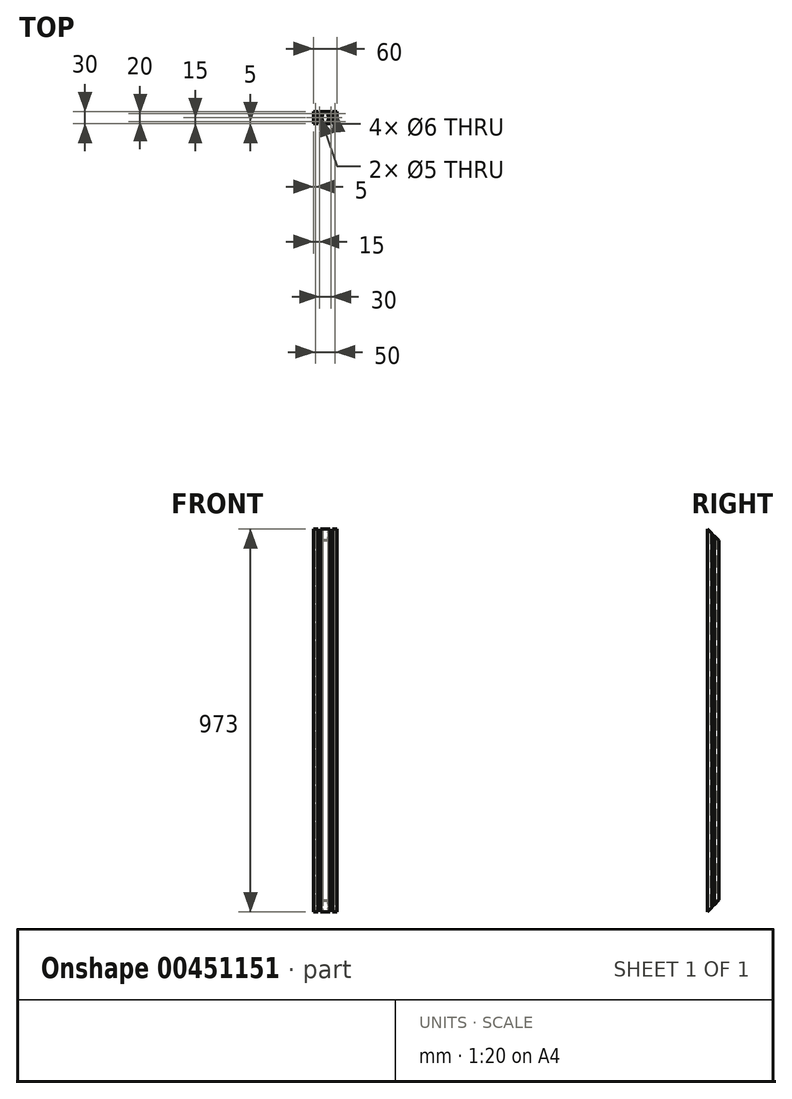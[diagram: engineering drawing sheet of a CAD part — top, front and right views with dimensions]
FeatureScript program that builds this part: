
annotation { "Feature Type Name" : "Feature", "Feature Type Description" : "" }
export const myFeature = defineFeature(function(context is Context, id is Id, definition is map)
    precondition{}
    {
        {
            var Q0;
            Q0=qCreatedBy(makeId("Top.planeOp"),FACE);
            var sketch = newSketch(context, id + "F0", { "sketchPlane" : qUnion([Q0])});
            skLineSegment(sketch, "E0.bottom", {"start": v(30, -15) * mm, "end": v(-30, -15) * mm});
            skLineSegment(sketch, "E0.top", {"start": v(30, 15) * mm, "end": v(-30, 15) * mm});
            skLineSegment(sketch, "E0.left", {"start": v(30, -15) * mm, "end": v(30, 15) * mm});
            skLineSegment(sketch, "E0.right", {"start": v(-30, -15) * mm, "end": v(-30, 15) * mm});
            skPoint(sketch, "E0.middle", {"position": v(0, 0) * mm});
            skLineSegment(sketch, "E1.top", {"start": v(-11.85, 15) * mm, "end": v(-18.15, 15) * mm});
            skLineSegment(sketch, "E1.left", {"start": v(-11.85, 12.5) * mm, "end": v(-11.85, 15) * mm});
            skLineSegment(sketch, "E1.right", {"start": v(-18.15, 12.5) * mm, "end": v(-18.15, 15) * mm});
            skPoint(sketch, "E1.middle", {"position": v(-15, 13.75) * mm});
            skLineSegment(sketch, "E2.bottom", {"start": v(-9.85, 12.5) * mm, "end": v(-11.85, 12.5) * mm});
            skLineSegment(sketch, "E2.left", {"start": v(-9.85, 12.5) * mm, "end": v(-9.85, 6.55) * mm});
            skLineSegment(sketch, "E2.right", {"start": v(-20.15, 12.5) * mm, "end": v(-20.15, 6.55) * mm});
            skPoint(sketch, "E2.middle", {"position": v(-15, 9.52) * mm});
            skArc(sketch, "E3", {"start": v(-20.15, 6.55) * mm, "mid": v(-15, 4.5) * mm, "end": v(-9.85, 6.55) * mm});
            skPoint(sketch, "E4.MirrorP", {"position": v(15, 9.52) * mm});
            skPoint(sketch, "E5.MirrorP", {"position": v(15, 13.75) * mm});
            skLineSegment(sketch, "E6.MirrorCS", {"start": v(11.85, 12.5) * mm, "end": v(11.85, 15) * mm});
            skLineSegment(sketch, "E7.MirrorCS", {"start": v(18.15, 12.5) * mm, "end": v(18.15, 15) * mm});
            skLineSegment(sketch, "E8.MirrorCS", {"start": v(9.85, 12.5) * mm, "end": v(11.85, 12.5) * mm});
            skLineSegment(sketch, "E9.MirrorCS", {"start": v(9.85, 12.5) * mm, "end": v(9.85, 6.55) * mm});
            skArc(sketch, "E10.MirrorCS", {"start": v(20.15, 6.55) * mm, "mid": v(15, 4.5) * mm, "end": v(9.85, 6.55) * mm});
            skLineSegment(sketch, "E11.MirrorCS", {"start": v(20.15, 12.5) * mm, "end": v(20.15, 6.55) * mm});
            skLineSegment(sketch, "E12.MirrorCS", {"start": v(11.85, 15) * mm, "end": v(18.15, 15) * mm});
            skLineSegment(sketch, "E13.trimOffspring", {"start": v(-18.15, 12.5) * mm, "end": v(-20.15, 12.5) * mm});
            skLineSegment(sketch, "E14.trimOffspring", {"start": v(18.15, 12.5) * mm, "end": v(20.15, 12.5) * mm});
            skCircle(sketch, "E15", {"center": v(-15, 0) * mm, "radius": 2.5 * mm});
            skCircle(sketch, "E16", {"center": v(-25, 10) * mm, "radius": 3 * mm});
            skCircle(sketch, "E17.MirrorC", {"center": v(25, 10) * mm, "radius": 3 * mm});
            skCircle(sketch, "E18.MirrorC", {"center": v(25, -10) * mm, "radius": 3 * mm});
            skCircle(sketch, "E19.MirrorC", {"center": v(-25, -10) * mm, "radius": 3 * mm});
            skCircle(sketch, "E20.MirrorC", {"center": v(15, 0) * mm, "radius": 2.5 * mm});
            skLineSegment(sketch, "E21", {"start": v(-7, 12.5) * mm, "end": v(0, 12.5) * mm});
            skLineSegment(sketch, "E22", {"start": v(-7, 12.5) * mm, "end": v(-7, 7) * mm});
            skLineSegment(sketch, "E23", {"start": v(-10, 0) * mm, "end": v(-7, 7) * mm});
            skLineSegment(sketch, "E24.MirrorCS", {"start": v(10, 0) * mm, "end": v(7, 7) * mm});
            skLineSegment(sketch, "E25.MirrorCS", {"start": v(7, 12.5) * mm, "end": v(0, 12.5) * mm});
            skLineSegment(sketch, "E26.MirrorCS", {"start": v(7, 12.5) * mm, "end": v(7, 7) * mm});
            skLineSegment(sketch, "E27.MirrorCS", {"start": v(-18.15, -12.5) * mm, "end": v(-20.15, -12.5) * mm});
            skLineSegment(sketch, "E28.MirrorCS", {"start": v(-9.85, -12.5) * mm, "end": v(-11.85, -12.5) * mm});
            skLineSegment(sketch, "E29.MirrorCS", {"start": v(-9.85, -12.5) * mm, "end": v(-9.85, -6.55) * mm});
            skPoint(sketch, "E30.MirrorP", {"position": v(-15, -13.75) * mm});
            skPoint(sketch, "E31.MirrorP", {"position": v(-15, -9.52) * mm});
            skLineSegment(sketch, "E32.MirrorCS", {"start": v(-18.15, -12.5) * mm, "end": v(-18.15, -15) * mm});
            skLineSegment(sketch, "E33.MirrorCS", {"start": v(-11.85, -15) * mm, "end": v(-18.15, -15) * mm});
            skLineSegment(sketch, "E34.MirrorCS", {"start": v(-20.15, -12.5) * mm, "end": v(-20.15, -6.55) * mm});
            skLineSegment(sketch, "E35.MirrorCS", {"start": v(-11.85, -12.5) * mm, "end": v(-11.85, -15) * mm});
            skArc(sketch, "E36.MirrorCS", {"start": v(-20.15, -6.55) * mm, "mid": v(-15, -4.5) * mm, "end": v(-9.85, -6.55) * mm});
            skLineSegment(sketch, "E37.MirrorCS", {"start": v(18.15, -12.5) * mm, "end": v(20.15, -12.5) * mm});
            skLineSegment(sketch, "E38.MirrorCS", {"start": v(9.85, -12.5) * mm, "end": v(11.85, -12.5) * mm});
            skPoint(sketch, "E39.MirrorP", {"position": v(15, -13.75) * mm});
            skPoint(sketch, "E40.MirrorP", {"position": v(15, -9.52) * mm});
            skLineSegment(sketch, "E41.MirrorCS", {"start": v(18.15, -12.5) * mm, "end": v(18.15, -15) * mm});
            skArc(sketch, "E42.MirrorCS", {"start": v(20.15, -6.55) * mm, "mid": v(15, -4.5) * mm, "end": v(9.85, -6.55) * mm});
            skLineSegment(sketch, "E43.MirrorCS", {"start": v(9.85, -12.5) * mm, "end": v(9.85, -6.55) * mm});
            skLineSegment(sketch, "E44.MirrorCS", {"start": v(11.85, -12.5) * mm, "end": v(11.85, -15) * mm});
            skLineSegment(sketch, "E45.MirrorCS", {"start": v(11.85, -15) * mm, "end": v(18.15, -15) * mm});
            skLineSegment(sketch, "E46.MirrorCS", {"start": v(20.15, -12.5) * mm, "end": v(20.15, -6.55) * mm});
            skLineSegment(sketch, "E47.MirrorCS", {"start": v(10, 0) * mm, "end": v(7, -7) * mm});
            skLineSegment(sketch, "E48.MirrorCS", {"start": v(7, -12.5) * mm, "end": v(7, -7) * mm});
            skLineSegment(sketch, "E49.MirrorCS", {"start": v(7, -12.5) * mm, "end": v(0, -12.5) * mm});
            skLineSegment(sketch, "E50.MirrorCS", {"start": v(-7, -12.5) * mm, "end": v(0, -12.5) * mm});
            skLineSegment(sketch, "E51.MirrorCS", {"start": v(-10, 0) * mm, "end": v(-7, -7) * mm});
            skLineSegment(sketch, "E52.MirrorCS", {"start": v(-7, -12.5) * mm, "end": v(-7, -7) * mm});
            skLineSegment(sketch, "E53.top", {"start": v(-30, 3.15) * mm, "end": v(-30, -3.15) * mm});
            skLineSegment(sketch, "E53.left", {"start": v(-27.5, 3.15) * mm, "end": v(-30, 3.15) * mm});
            skLineSegment(sketch, "E53.right", {"start": v(-27.5, -3.15) * mm, "end": v(-30, -3.15) * mm});
            skLineSegment(sketch, "E54.bottom", {"start": v(-27.5, 5.15) * mm, "end": v(-27.5, 3.15) * mm});
            skLineSegment(sketch, "E54.left", {"start": v(-27.5, 5.15) * mm, "end": v(-21.55, 5.15) * mm});
            skLineSegment(sketch, "E54.right", {"start": v(-27.5, -5.15) * mm, "end": v(-21.55, -5.15) * mm});
            skArc(sketch, "E55", {"start": v(-21.55, -5.15) * mm, "mid": v(-19.5, 0) * mm, "end": v(-21.55, 5.15) * mm});
            skLineSegment(sketch, "E56.trimOffspring", {"start": v(-27.5, -3.15) * mm, "end": v(-27.5, -5.15) * mm});
            skArc(sketch, "E57.MirrorCS", {"start": v(21.55, -5.15) * mm, "mid": v(19.5, 0) * mm, "end": v(21.55, 5.15) * mm});
            skLineSegment(sketch, "E58.MirrorCS", {"start": v(27.5, -5.15) * mm, "end": v(21.55, -5.15) * mm});
            skLineSegment(sketch, "E59.MirrorCS", {"start": v(30, 3.15) * mm, "end": v(30, -3.15) * mm});
            skLineSegment(sketch, "E60.MirrorCS", {"start": v(27.5, -3.15) * mm, "end": v(30, -3.15) * mm});
            skLineSegment(sketch, "E61.MirrorCS", {"start": v(27.5, 5.15) * mm, "end": v(27.5, 3.15) * mm});
            skLineSegment(sketch, "E62.MirrorCS", {"start": v(27.5, 3.15) * mm, "end": v(30, 3.15) * mm});
            skLineSegment(sketch, "E63.MirrorCS", {"start": v(27.5, 5.15) * mm, "end": v(21.55, 5.15) * mm});
            skLineSegment(sketch, "E64.MirrorCS", {"start": v(27.5, -3.15) * mm, "end": v(27.5, -5.15) * mm});
            skSolve(sketch);
        }
        {
            var Q0;
            {var subQ30=sQuery(id+"F0.wireOp",EDGE,"E1.left");Q0=makeQuery(id+"F0.imprint","IMPRINT",FACE,{"disambiguationData":[TD([[makeQuery(id+"F0.imprint","IMPRINT",EDGE,{"derivedFrom":subQ30}),-1.0]])]});}
            extrude(context, id + "F1", {"entities" : qUnion([Q0]), "offsetDistance" : 25 * mm, "depth" : 973 * mm});
        }
        {
            var Q0;
            Q0=makeQuery(id+"F1.opExtrude","SWEPT_EDGE",EDGE,{"disambiguationData":[OSD([sQuery(id+"F0.wireOp",EDGE,"E21"),sQuery(id+"F0.wireOp",EDGE,"E22")])]});
            var Q1;
            Q1=makeQuery(id+"F1.opExtrude","SWEPT_EDGE",EDGE,{"disambiguationData":[OSD([sQuery(id+"F0.wireOp",EDGE,"E25.MirrorCS"),sQuery(id+"F0.wireOp",EDGE,"E26.MirrorCS")])]});
            var Q2;
            Q2=makeQuery(id+"F1.opExtrude","SWEPT_EDGE",EDGE,{"disambiguationData":[OSD([sQuery(id+"F0.wireOp",EDGE,"840db5bc-c403-45cd-90c7-254e62d9e8c5.3.2"),sQuery(id+"F0.wireOp",EDGE,"840db5bc-c403-45cd-90c7-254e62d9e8c5.3.3")])]});
            var Q3;
            Q3=makeQuery(id+"F1.opExtrude","SWEPT_EDGE",EDGE,{"disambiguationData":[OSD([sQuery(id+"F0.wireOp",EDGE,"840db5bc-c403-45cd-90c7-254e62d9e8c5.3.4"),sQuery(id+"F0.wireOp",EDGE,"840db5bc-c403-45cd-90c7-254e62d9e8c5.3.5")])]});
            var Q4;
            Q4=makeQuery(id+"F1.opExtrude","SWEPT_EDGE",EDGE,{"disambiguationData":[OSD([sQuery(id+"F0.wireOp",EDGE,"840db5bc-c403-45cd-90c7-254e62d9e8c5.1.4"),sQuery(id+"F0.wireOp",EDGE,"840db5bc-c403-45cd-90c7-254e62d9e8c5.1.5")])]});
            var Q5;
            Q5=makeQuery(id+"F1.opExtrude","SWEPT_EDGE",EDGE,{"disambiguationData":[OSD([sQuery(id+"F0.wireOp",EDGE,"840db5bc-c403-45cd-90c7-254e62d9e8c5.1.2"),sQuery(id+"F0.wireOp",EDGE,"840db5bc-c403-45cd-90c7-254e62d9e8c5.1.3")])]});
            var Q6;
            Q6=makeQuery(id+"F1.opExtrude","SWEPT_EDGE",EDGE,{"disambiguationData":[OSD([sQuery(id+"F0.wireOp",EDGE,"840db5bc-c403-45cd-90c7-254e62d9e8c5.2.2"),sQuery(id+"F0.wireOp",EDGE,"840db5bc-c403-45cd-90c7-254e62d9e8c5.2.3")])]});
            var Q7;
            Q7=makeQuery(id+"F1.opExtrude","SWEPT_EDGE",EDGE,{"disambiguationData":[OSD([sQuery(id+"F0.wireOp",EDGE,"840db5bc-c403-45cd-90c7-254e62d9e8c5.2.4"),sQuery(id+"F0.wireOp",EDGE,"840db5bc-c403-45cd-90c7-254e62d9e8c5.2.5")])]});
            fillet(context, id + "F2", {"entities" : qUnion([Q0, Q1, Q2, Q3, Q4, Q5, Q6, Q7]), "radius" : 2 * mm, "tangentPropagation" : true, "allowEdgeOverflow" : false});
        }
        {
            var Q0;
            Q0=makeQuery(id+"F1.opExtrude","SWEPT_EDGE",EDGE,{"disambiguationData":[OSD([sQuery(id+"F0.wireOp",EDGE,"DFmKlNwq-wdCH-8nxe-YtyU-4GV9lN6q6mBF"),sQuery(id+"F0.wireOp",EDGE,"E23")])]});
            var Q1;
            Q1=makeQuery(id+"F1.opExtrude","SWEPT_EDGE",EDGE,{"disambiguationData":[OSD([sQuery(id+"F0.wireOp",EDGE,"666cdc41-9f22-4022-b962-67eb0134baf70.MirrorCS"),sQuery(id+"F0.wireOp",EDGE,"E24.MirrorCS")])]});
            var Q2;
            Q2=makeQuery(id+"F1.opExtrude","SWEPT_EDGE",EDGE,{"disambiguationData":[OSD([sQuery(id+"F0.wireOp",EDGE,"840db5bc-c403-45cd-90c7-254e62d9e8c5.3.0"),sQuery(id+"F0.wireOp",EDGE,"840db5bc-c403-45cd-90c7-254e62d9e8c5.3.1")])]});
            var Q3;
            Q3=makeQuery(id+"F1.opExtrude","SWEPT_EDGE",EDGE,{"disambiguationData":[OSD([sQuery(id+"F0.wireOp",EDGE,"840db5bc-c403-45cd-90c7-254e62d9e8c5.1.6"),sQuery(id+"F0.wireOp",EDGE,"840db5bc-c403-45cd-90c7-254e62d9e8c5.1.7")])]});
            var Q4;
            Q4=makeQuery(id+"F1.opExtrude","SWEPT_EDGE",EDGE,{"disambiguationData":[OSD([sQuery(id+"F0.wireOp",EDGE,"840db5bc-c403-45cd-90c7-254e62d9e8c5.1.0"),sQuery(id+"F0.wireOp",EDGE,"840db5bc-c403-45cd-90c7-254e62d9e8c5.1.1")])]});
            var Q5;
            Q5=makeQuery(id+"F1.opExtrude","SWEPT_EDGE",EDGE,{"disambiguationData":[OSD([sQuery(id+"F0.wireOp",EDGE,"840db5bc-c403-45cd-90c7-254e62d9e8c5.3.6"),sQuery(id+"F0.wireOp",EDGE,"840db5bc-c403-45cd-90c7-254e62d9e8c5.3.7")])]});
            var Q6;
            Q6=makeQuery(id+"F1.opExtrude","SWEPT_EDGE",EDGE,{"disambiguationData":[OSD([sQuery(id+"F0.wireOp",EDGE,"840db5bc-c403-45cd-90c7-254e62d9e8c5.2.0"),sQuery(id+"F0.wireOp",EDGE,"840db5bc-c403-45cd-90c7-254e62d9e8c5.2.1")])]});
            var Q7;
            Q7=makeQuery(id+"F1.opExtrude","SWEPT_EDGE",EDGE,{"disambiguationData":[OSD([sQuery(id+"F0.wireOp",EDGE,"840db5bc-c403-45cd-90c7-254e62d9e8c5.2.6"),sQuery(id+"F0.wireOp",EDGE,"840db5bc-c403-45cd-90c7-254e62d9e8c5.2.7")])]});
            fillet(context, id + "F3", {"entities" : qUnion([Q0, Q1, Q2, Q3, Q4, Q5, Q6, Q7]), "radius" : 7 * mm, "tangentPropagation" : true, "allowEdgeOverflow" : false});
        }
        {
            var Q0;
            Q0=qCreatedBy(makeId("Right.planeOp"),FACE);
            var sketch = newSketch(context, id + "F4", { "sketchPlane" : qUnion([Q0])});
            skLineSegment(sketch, "E65", {"start": v(-15, 0) * mm, "end": v(15, 30) * mm});
            skLineSegment(sketch, "E66", {"start": v(15, 30) * mm, "end": v(15, 0) * mm});
            skLineSegment(sketch, "E67", {"start": v(15, 0) * mm, "end": v(-15, 0) * mm});
            skLineSegment(sketch, "E68", {"start": v(-15, 973) * mm, "end": v(15, 973) * mm});
            skLineSegment(sketch, "E69", {"start": v(15, 973) * mm, "end": v(15, 943) * mm});
            skLineSegment(sketch, "E70", {"start": v(15, 943) * mm, "end": v(-15, 973) * mm});
            skSolve(sketch);
        }
        {
            var Q0;
            Q0 = qSketchRegion(id + "F4", true);
            extrude(context, id + "F5", {"entities" : qUnion([Q0]), "operationType" : NewBodyOperationType.REMOVE, "oppositeDirection" : true, "depth" : 60 * mm, "offsetDistance" : 25 * mm, "symmetric" : true});
        }
    });
